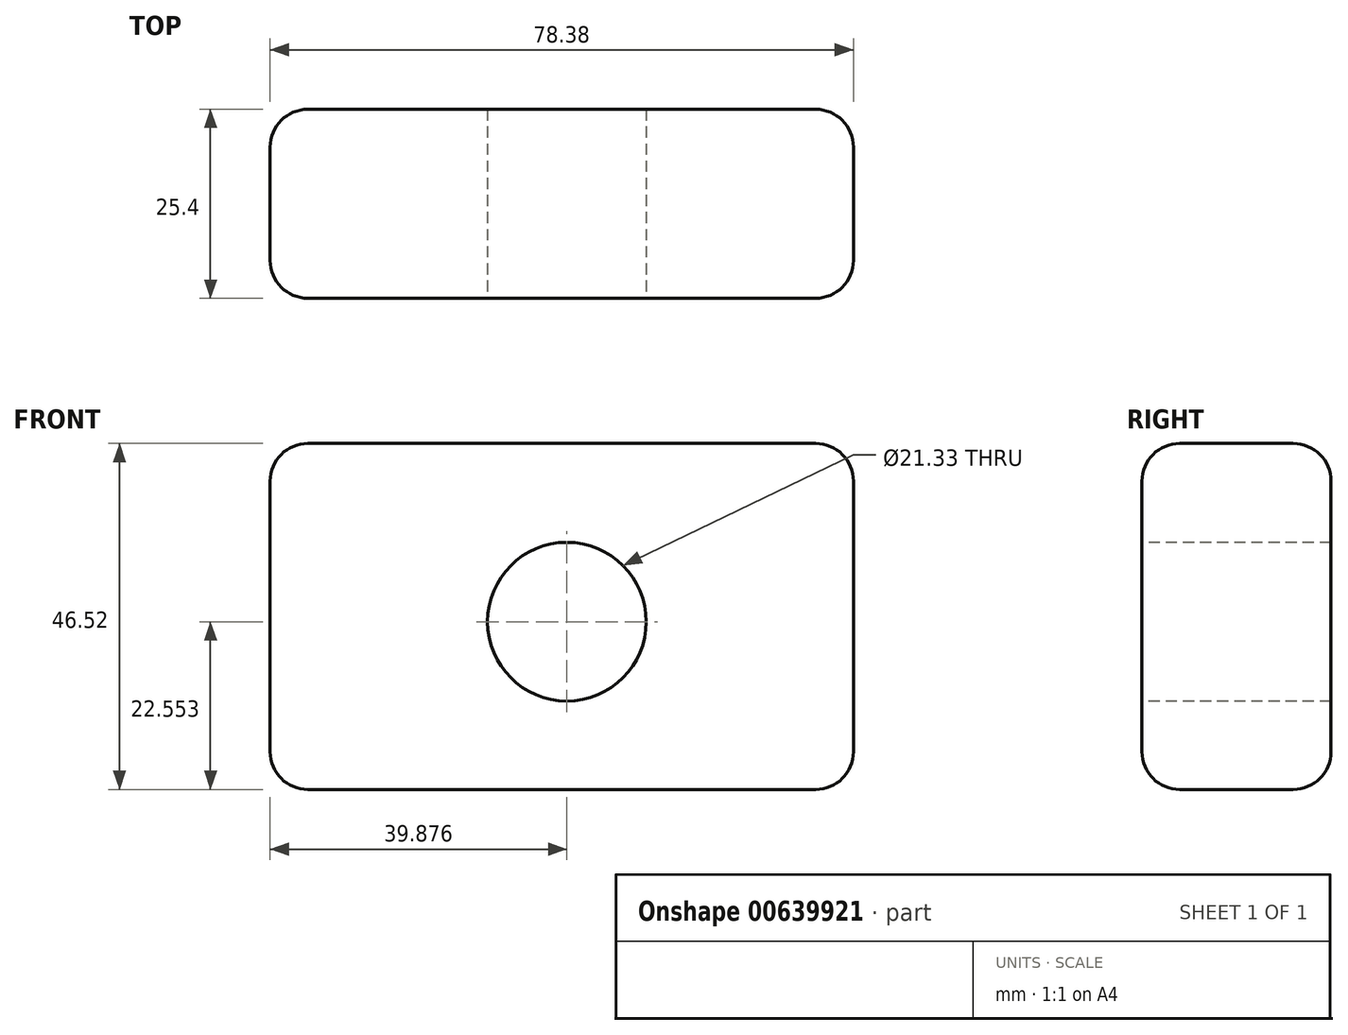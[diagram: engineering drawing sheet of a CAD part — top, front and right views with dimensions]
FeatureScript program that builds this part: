
annotation { "Feature Type Name" : "Feature", "Feature Type Description" : "" }
export const myFeature = defineFeature(function(context is Context, id is Id, definition is map)
    precondition{}
    {
        {
            var Q0;
            Q0=qCreatedBy(makeId("Front.planeOp"),FACE);
            var sketch = newSketch(context, id + "F0", { "sketchPlane" : qUnion([Q0])});
            skLineSegment(sketch, "E0.bottom", {"start": v(-37.33, 26.17) * mm, "end": v(41.05, 26.17) * mm});
            skLineSegment(sketch, "E0.top", {"start": v(-37.33, -20.35) * mm, "end": v(41.05, -20.35) * mm});
            skLineSegment(sketch, "E0.left", {"start": v(-37.33, 26.17) * mm, "end": v(-37.33, -20.35) * mm});
            skLineSegment(sketch, "E0.right", {"start": v(41.05, 26.17) * mm, "end": v(41.05, -20.35) * mm});
            skSolve(sketch);
        }
        {
            var Q0;
            Q0=makeQuery(id+"F0.imprint","IMPRINT",FACE,{"disambiguationData":[TD([[makeQuery(id+"F0.imprint","IMPRINT",EDGE,{"derivedFrom":sQuery(id+"F0.wireOp",EDGE,"E0.bottom")}),-1.0]])]});
            extrude(context, id + "F1", {"entities" : qUnion([Q0]), "depth" : 25.4 * mm, "offsetDistance" : 25.4 * mm});
        }
        {
            var Q0;
            Q0=makeQuery(id+"F1.opExtrude","SWEPT_EDGE",EDGE,{"disambiguationData":[OSD([sQuery(id+"F0.wireOp",EDGE,"E0.bottom"),sQuery(id+"F0.wireOp",EDGE,"E0.right")])]});
            var Q1;
            Q1=makeQuery(id+"F1.opExtrude","CAP_EDGE",EDGE,{"disambiguationData":[OSD([sQuery(id+"F0.wireOp",EDGE,"E0.bottom")])],"isStart":false});
            var Q2;
            Q2=makeQuery(id+"F1.opExtrude","CAP_EDGE",EDGE,{"disambiguationData":[OSD([sQuery(id+"F0.wireOp",EDGE,"E0.bottom")])],"isStart":true});
            var Q3;
            Q3=makeQuery(id+"F1.opExtrude","CAP_EDGE",EDGE,{"disambiguationData":[OSD([sQuery(id+"F0.wireOp",EDGE,"E0.right")])],"isStart":false});
            var Q4;
            Q4=makeQuery(id+"F1.opExtrude","CAP_EDGE",EDGE,{"disambiguationData":[OSD([sQuery(id+"F0.wireOp",EDGE,"E0.right")])],"isStart":true});
            var Q5;
            Q5=makeQuery(id+"F1.opExtrude","CAP_EDGE",EDGE,{"disambiguationData":[OSD([sQuery(id+"F0.wireOp",EDGE,"E0.left")])],"isStart":true});
            var Q6;
            Q6=makeQuery(id+"F1.opExtrude","CAP_EDGE",EDGE,{"disambiguationData":[OSD([sQuery(id+"F0.wireOp",EDGE,"E0.top")])],"isStart":true});
            var Q7;
            Q7=makeQuery(id+"F1.opExtrude","SWEPT_EDGE",EDGE,{"disambiguationData":[OSD([sQuery(id+"F0.wireOp",EDGE,"E0.top"),sQuery(id+"F0.wireOp",EDGE,"E0.right")])]});
            var Q8;
            Q8=makeQuery(id+"F1.opExtrude","SWEPT_EDGE",EDGE,{"disambiguationData":[OSD([sQuery(id+"F0.wireOp",EDGE,"E0.top"),sQuery(id+"F0.wireOp",EDGE,"E0.left")])]});
            var Q9;
            Q9=makeQuery(id+"F1.opExtrude","CAP_EDGE",EDGE,{"disambiguationData":[OSD([sQuery(id+"F0.wireOp",EDGE,"E0.left")])],"isStart":false});
            var Q10;
            Q10=makeQuery(id+"F1.opExtrude","CAP_EDGE",EDGE,{"disambiguationData":[OSD([sQuery(id+"F0.wireOp",EDGE,"E0.top")])],"isStart":false});
            fillet(context, id + "F2", {"entities" : qUnion([Q0, Q1, Q2, Q3, Q4, Q5, Q6, Q7, Q8, Q9, Q10]), "radius" : 5.08 * mm, "tangentPropagation" : true, "allowEdgeOverflow" : false});
        }
        {
            var Q0;
            Q0=makeQuery(id+"F1.opExtrude","SWEPT_EDGE",EDGE,{"disambiguationData":[OSD([sQuery(id+"F0.wireOp",EDGE,"E0.bottom"),sQuery(id+"F0.wireOp",EDGE,"E0.left")])]});
            fillet(context, id + "F3", {"entities" : qUnion([Q0]), "radius" : 5.08 * mm, "tangentPropagation" : true, "allowEdgeOverflow" : false});
        }
        {
            var Q0;
            Q0=makeQuery(id+"F1.opExtrude","CAP_FACE",FACE,{"disambiguationData":[OSD([sQuery(id+"F0.wireOp",EDGE,"E0.bottom"),sQuery(id+"F0.wireOp",EDGE,"E0.top"),sQuery(id+"F0.wireOp",EDGE,"E0.left"),sQuery(id+"F0.wireOp",EDGE,"E0.right")])],"isStart":false});
            var sketch = newSketch(context, id + "F4", { "sketchPlane" : qUnion([Q0])});
            skCircle(sketch, "E1", {"center": v(2.55, 2.2) * mm, "radius": 10.67 * mm});
            skSolve(sketch);
        }
        {
            var Q0;
            Q0=makeQuery(id+"F4.imprint","IMPRINT",FACE,{"disambiguationData":[TD([[makeQuery(id+"F4.imprint","IMPRINT",EDGE,{"derivedFrom":sQuery(id+"F4.wireOp",EDGE,"E1")}),1.0]])]});
            var Q1;
            Q1=sQuery(id+"F4.wireOp",EDGE,"E1");
            extrude(context, id + "F5", {"entities" : qUnion([Q0]), "operationType" : NewBodyOperationType.REMOVE, "surfaceEntities" : qUnion([Q1]), "endBound" : BoundingType.UP_TO_NEXT, "oppositeDirection" : true, "depth" : 25.4 * mm, "offsetDistance" : 25.4 * mm});
        }
    });
